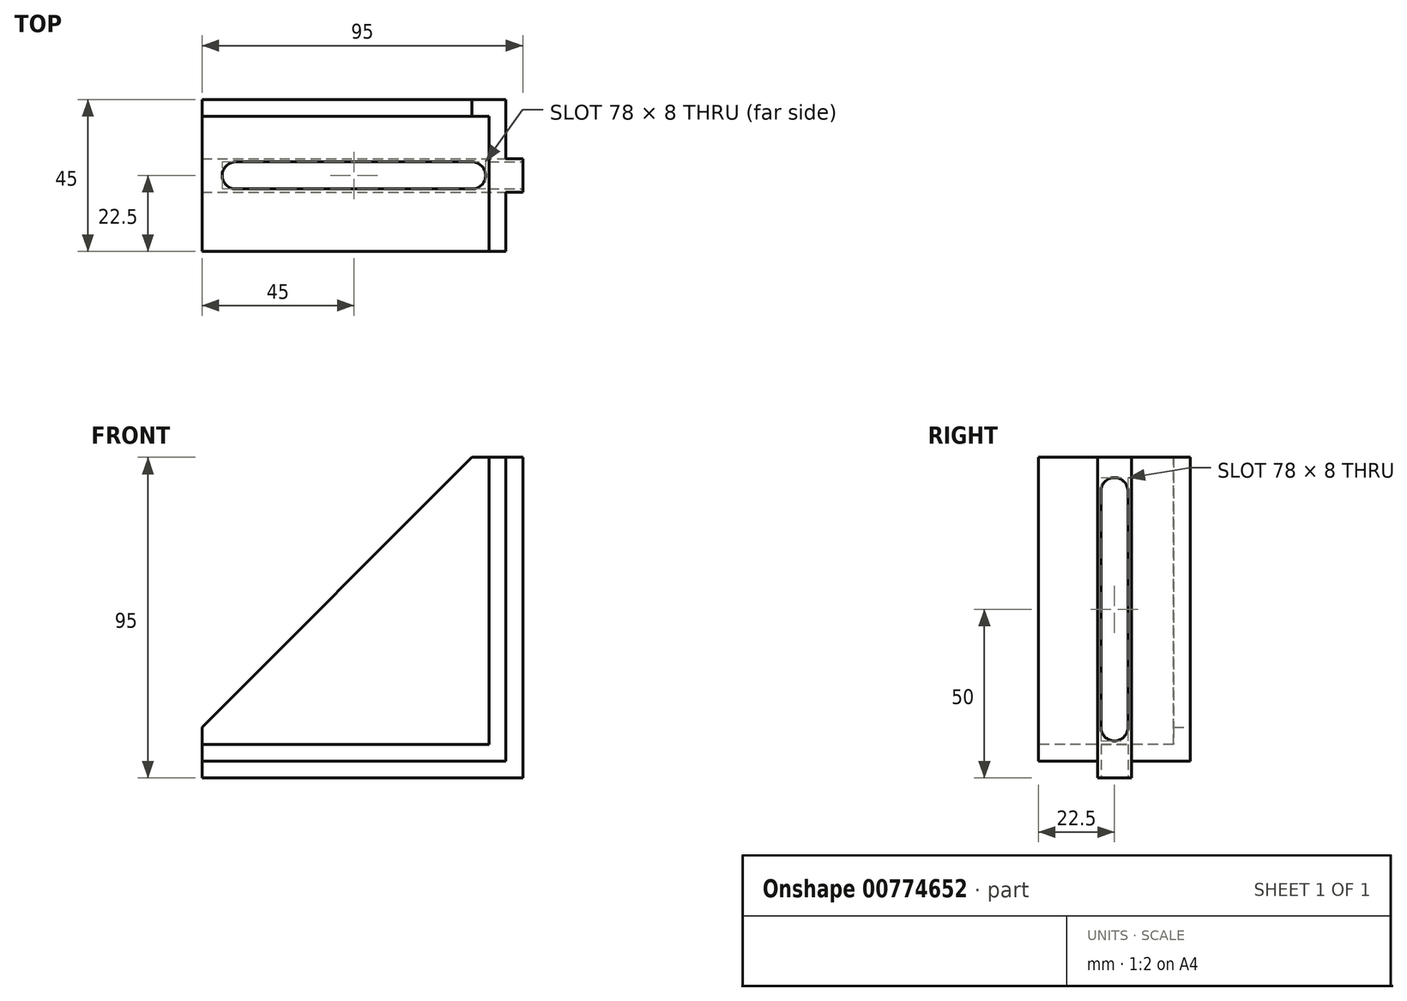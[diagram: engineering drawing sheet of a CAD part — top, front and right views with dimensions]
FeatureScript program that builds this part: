
annotation { "Feature Type Name" : "Feature", "Feature Type Description" : "" }
export const myFeature = defineFeature(function(context is Context, id is Id, definition is map)
    precondition{}
    {
        {
            var Q0;
            Q0=qCreatedBy(makeId("Front.planeOp"),FACE);
            var sketch = newSketch(context, id + "F0", { "sketchPlane" : qUnion([Q0])});
            skLineSegment(sketch, "E0", {"start": v(-90, 0) * mm, "end": v(0, 0) * mm});
            skLineSegment(sketch, "E1", {"start": v(0, 0) * mm, "end": v(0, 90) * mm});
            skLineSegment(sketch, "E2", {"start": v(0, 90) * mm, "end": v(-10, 90) * mm});
            skLineSegment(sketch, "E3", {"start": v(-10, 90) * mm, "end": v(-90, 10) * mm});
            skLineSegment(sketch, "E4", {"start": v(-90, 10) * mm, "end": v(-90, 0) * mm});
            skSolve(sketch);
        }
        {
            var Q0;
            Q0 = qSketchRegion(id + "F0", true);
            extrude(context, id + "F1", {"entities" : qUnion([Q0]), "depth" : 45 * mm, "offsetDistance" : 25 * mm});
        }
        {
            var Q0;
            Q0=makeQuery(id+"F1.opExtrude","CAP_FACE",FACE,{"disambiguationData":[OSD([sQuery(id+"F0.wireOp",EDGE,"E0"),sQuery(id+"F0.wireOp",EDGE,"E1"),sQuery(id+"F0.wireOp",EDGE,"E2"),sQuery(id+"F0.wireOp",EDGE,"E3"),sQuery(id+"F0.wireOp",EDGE,"E4")])],"isStart":false});
            var sketch = newSketch(context, id + "F2", { "sketchPlane" : qUnion([Q0])});
            skLineSegment(sketch, "E5", {"start": v(-90, 10) * mm, "end": v(-90, 5) * mm});
            skLineSegment(sketch, "E6", {"start": v(-90, 5) * mm, "end": v(-5, 5) * mm});
            skLineSegment(sketch, "E7", {"start": v(-5, 5) * mm, "end": v(-5, 90) * mm});
            skLineSegment(sketch, "E8", {"start": v(-5, 90) * mm, "end": v(-10, 90) * mm});
            skLineSegment(sketch, "E9", {"start": v(-10, 90) * mm, "end": v(-90, 10) * mm});
            skSolve(sketch);
        }
        {
            var Q0;
            Q0 = qSketchRegion(id + "F2", true);
            extrude(context, id + "F3", {"entities" : qUnion([Q0]), "operationType" : NewBodyOperationType.REMOVE, "oppositeDirection" : true, "depth" : 40 * mm, "offsetDistance" : 25 * mm});
        }
        {
            var Q0;
            Q0=makeQuery(id+"F1.opExtrude","SWEPT_FACE",FACE,{"disambiguationData":[OSD([sQuery(id+"F0.wireOp",EDGE,"E0")])]});
            var sketch = newSketch(context, id + "F4", { "sketchPlane" : qUnion([Q0])});
            skLineSegment(sketch, "E10.bottom", {"start": v(-90, 27.5) * mm, "end": v(0, 27.5) * mm});
            skLineSegment(sketch, "E10.top", {"start": v(-90, 17.5) * mm, "end": v(0, 17.5) * mm});
            skLineSegment(sketch, "E10.left", {"start": v(-90, 27.5) * mm, "end": v(-90, 17.5) * mm});
            skLineSegment(sketch, "E10.right", {"start": v(0, 27.5) * mm, "end": v(0, 17.5) * mm});
            skLineSegment(sketch, "E11", {"start": v(-119.35, 22.5) * mm, "end": v(15.23, 22.5) * mm, "construction": true});
            skSolve(sketch);
        }
        {
            var Q0;
            Q0 = qSketchRegion(id + "F4", true);
            extrude(context, id + "F5", {"entities" : qUnion([Q0]), "operationType" : NewBodyOperationType.ADD, "depth" : 5 * mm, "offsetDistance" : 25 * mm});
        }
        {
            var Q0;
            Q0=makeQuery(id+"F5.boolean.opBoolean","MERGE",FACE,{"derivedFrom":[makeQuery(id+"F1.opExtrude","SWEPT_FACE",FACE,{"disambiguationData":[OSD([sQuery(id+"F0.wireOp",EDGE,"E1")])]}),makeQuery(id+"F5.opExtrude","SWEPT_FACE",FACE,{"disambiguationData":[OSD([sQuery(id+"F4.wireOp",EDGE,"E10.right")])]})]});
            var sketch = newSketch(context, id + "F6", { "sketchPlane" : qUnion([Q0])});
            skLineSegment(sketch, "E12.bottom", {"start": v(-27.5, -5) * mm, "end": v(-17.5, -5) * mm});
            skLineSegment(sketch, "E12.top", {"start": v(-27.5, 90) * mm, "end": v(-17.5, 90) * mm});
            skLineSegment(sketch, "E12.left", {"start": v(-27.5, -5) * mm, "end": v(-27.5, 90) * mm});
            skLineSegment(sketch, "E12.right", {"start": v(-17.5, -5) * mm, "end": v(-17.5, 90) * mm});
            skSolve(sketch);
        }
        {
            var Q0;
            Q0 = qSketchRegion(id + "F6", true);
            extrude(context, id + "F7", {"entities" : qUnion([Q0]), "operationType" : NewBodyOperationType.ADD, "depth" : 5 * mm, "offsetDistance" : 25 * mm});
        }
        {
            var Q0;
            Q0=makeQuery(id+"F7.opExtrude","CAP_FACE",FACE,{"disambiguationData":[OSD([sQuery(id+"F6.wireOp",EDGE,"E12.bottom"),sQuery(id+"F6.wireOp",EDGE,"E12.top"),sQuery(id+"F6.wireOp",EDGE,"E12.left"),sQuery(id+"F6.wireOp",EDGE,"E12.right")])],"isStart":false});
            var sketch = newSketch(context, id + "F8", { "sketchPlane" : qUnion([Q0])});
            skLineSegment(sketch, "E13", {"start": v(-22.5, 92.39) * mm, "end": v(-22.5, -14.85) * mm, "construction": true});
            skArc(sketch, "E14", {"start": v(-26.5, 80) * mm, "mid": v(-22.5, 84) * mm, "end": v(-18.5, 80) * mm});
            skArc(sketch, "E15", {"start": v(-26.5, 9.96) * mm, "mid": v(-22.5, 6) * mm, "end": v(-18.5, 9.96) * mm});
            skLineSegment(sketch, "E16", {"start": v(-26.5, 80) * mm, "end": v(-26.5, 9.96) * mm});
            skLineSegment(sketch, "E17", {"start": v(-18.5, 9.96) * mm, "end": v(-18.5, 80) * mm});
            skLineSegment(sketch, "E18", {"start": v(-66.27, 45) * mm, "end": v(13.73, 45) * mm, "construction": true});
            skSolve(sketch);
        }
        {
            var Q0;
            Q0 = qSketchRegion(id + "F8", true);
            extrude(context, id + "F9", {"entities" : qUnion([Q0]), "operationType" : NewBodyOperationType.REMOVE, "endBound" : BoundingType.UP_TO_NEXT, "oppositeDirection" : true, "depth" : 25 * mm, "offsetDistance" : 25 * mm});
        }
        {
            var Q0;
            Q0=makeQuery(id+"F7.boolean.opBoolean","MERGE",FACE,{"derivedFrom":[makeQuery(id+"F5.opExtrude","CAP_FACE",FACE,{"disambiguationData":[OSD([sQuery(id+"F4.wireOp",EDGE,"E10.bottom"),sQuery(id+"F4.wireOp",EDGE,"E10.top"),sQuery(id+"F4.wireOp",EDGE,"E10.left"),sQuery(id+"F4.wireOp",EDGE,"E10.right")])],"isStart":false}),makeQuery(id+"F7.opExtrude","SWEPT_FACE",FACE,{"disambiguationData":[OSD([sQuery(id+"F6.wireOp",EDGE,"E12.bottom")])]})]});
            var sketch = newSketch(context, id + "F10", { "sketchPlane" : qUnion([Q0])});
            skLineSegment(sketch, "E19", {"start": v(-96.91, 22.5) * mm, "end": v(20.94, 22.5) * mm, "construction": true});
            skLineSegment(sketch, "E20", {"start": v(-45, 53.2) * mm, "end": v(-45, -5.62) * mm, "construction": true});
            skArc(sketch, "E21", {"start": v(-80, 18.5) * mm, "mid": v(-84, 22.5) * mm, "end": v(-80, 26.5) * mm});
            skArc(sketch, "E22", {"start": v(-10, 26.5) * mm, "mid": v(-6, 22.5) * mm, "end": v(-10, 18.5) * mm});
            skLineSegment(sketch, "E23", {"start": v(-80, 18.5) * mm, "end": v(-10, 18.5) * mm});
            skLineSegment(sketch, "E24", {"start": v(-10, 26.5) * mm, "end": v(-80, 26.5) * mm});
            skSolve(sketch);
        }
        {
            var Q0;
            Q0 = qSketchRegion(id + "F10", true);
            extrude(context, id + "F11", {"entities" : qUnion([Q0]), "operationType" : NewBodyOperationType.REMOVE, "endBound" : BoundingType.UP_TO_NEXT, "oppositeDirection" : true, "depth" : 25 * mm, "offsetDistance" : 25 * mm});
        }
    });
